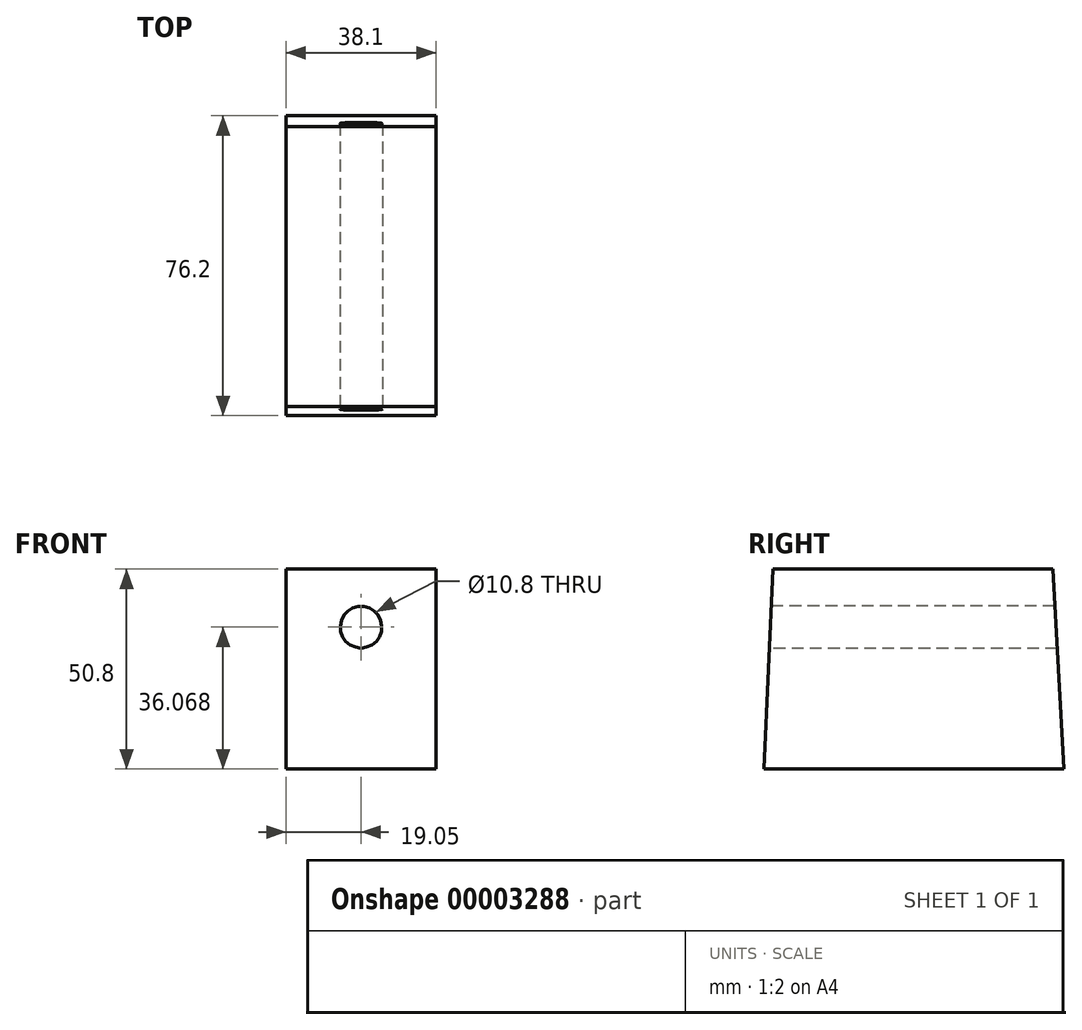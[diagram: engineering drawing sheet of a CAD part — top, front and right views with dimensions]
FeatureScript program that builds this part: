
annotation { "Feature Type Name" : "Feature", "Feature Type Description" : "" }
export const myFeature = defineFeature(function(context is Context, id is Id, definition is map)
    precondition{}
    {
        {
            var Q0;
            Q0=qCreatedBy(makeId("Top.planeOp"),FACE);
            var sketch = newSketch(context, id + "F0", { "sketchPlane" : qUnion([Q0])});
            skLineSegment(sketch, "E0", {"start": v(0, 0) * mm, "end": v(0, 76.2) * mm});
            skLineSegment(sketch, "E1", {"start": v(0, 76.2) * mm, "end": v(38.1, 76.2) * mm});
            skLineSegment(sketch, "E2", {"start": v(38.1, 76.2) * mm, "end": v(38.1, 0) * mm});
            skLineSegment(sketch, "E3", {"start": v(0, 0) * mm, "end": v(38.1, 0) * mm});
            skLineSegment(sketch, "E4", {"start": v(19.05, 0) * mm, "end": v(19.05, 76.2) * mm, "construction": true});
            skSolve(sketch);
        }
        {
            var Q0;
            Q0=makeQuery(id+"F0.imprint","IMPRINT",FACE,{"disambiguationData":[TD([[makeQuery(id+"F0.imprint","IMPRINT",EDGE,{"derivedFrom":sQuery(id+"F0.wireOp",EDGE,"E0")}),-1.0]])]});
            extrude(context, id + "F1", {"entities" : qUnion([Q0]), "depth" : 50.8 * mm});
        }
        {
            var Q0;
            Q0=makeQuery(id+"F1.opExtrude","SWEPT_FACE",FACE,{"disambiguationData":[OSD([sQuery(id+"F0.wireOp",EDGE,"E3")])]});
            var sketch = newSketch(context, id + "F2", { "sketchPlane" : qUnion([Q0])});
            skCircle(sketch, "E5", {"center": v(19.05, 36.07) * mm, "radius": 5.4 * mm});
            skCircle(sketch, "E6.0", {"center": v(19.05, 36.07) * mm, "radius": 11.75 * mm});
            skLineSegment(sketch, "E7", {"start": v(19.05, 50.8) * mm, "end": v(19.05, 0) * mm, "construction": true});
            skLineSegment(sketch, "E8", {"start": v(0, 22.73) * mm, "end": v(38.1, 22.73) * mm});
            skLineSegment(sketch, "E9", {"start": v(7.48, 38.11) * mm, "end": v(4.76, 22.73) * mm});
            skLineSegment(sketch, "E10", {"start": v(30.62, 38.11) * mm, "end": v(33.34, 22.73) * mm});
            skSolve(sketch);
        }
        {
            var Q0;
            Q0=makeQuery(id+"F2.imprint","IMPRINT",FACE,{"disambiguationData":[TD([[makeQuery(id+"F2.imprint","IMPRINT",EDGE,{"derivedFrom":sQuery(id+"F2.wireOp",EDGE,"E5")}),1.0]])]});
            var Q1;
            Q1=sQuery(id+"F2.wireOp",EDGE,"E5");
            extrude(context, id + "F3", {"entities" : qUnion([Q0]), "operationType" : NewBodyOperationType.REMOVE, "surfaceEntities" : qUnion([Q1]), "endBound" : BoundingType.THROUGH_ALL, "oppositeDirection" : true, "depth" : 25.4 * mm});
        }
        {
            var Q0;
            Q0=makeQuery(id+"F1.opExtrude","SWEPT_FACE",FACE,{"disambiguationData":[OSD([sQuery(id+"F0.wireOp",EDGE,"E1")])]});
            var sketch = newSketch(context, id + "F4", { "sketchPlane" : qUnion([Q0])});
            skSolve(sketch);
        }
        {
            var Q0;
            Q0=makeQuery(id+"F1.opExtrude","SWEPT_FACE",FACE,{"disambiguationData":[OSD([sQuery(id+"F0.wireOp",EDGE,"E2")])]});
            var sketch = newSketch(context, id + "F5", { "sketchPlane" : qUnion([Q0])});
            skLineSegment(sketch, "E11", {"start": v(73.4, 50.8) * mm, "end": v(76.2, 0) * mm});
            skLineSegment(sketch, "E12", {"start": v(2.3, 50.8) * mm, "end": v(0, 0) * mm});
            skSolve(sketch);
        }
        {
            var Q0;
            {var subQ2=sQuery(id+"F5.wireOp",EDGE,"E12");Q0=makeQuery(id+"F5.imprint","IMPRINT",FACE,{"disambiguationData":[TD([[makeQuery(id+"F5.imprint","IMPRINT",EDGE,{"derivedFrom":subQ2}),-1.0]])]});}
            var Q1;
            {var subQ2=sQuery(id+"F5.wireOp",EDGE,"E11");Q1=makeQuery(id+"F5.imprint","IMPRINT",FACE,{"disambiguationData":[TD([[makeQuery(id+"F5.imprint","IMPRINT",EDGE,{"derivedFrom":subQ2}),1.0]])]});}
            extrude(context, id + "F6", {"entities" : qUnion([Q0, Q1]), "operationType" : NewBodyOperationType.REMOVE, "oppositeDirection" : true, "depth" : 50.8 * mm});
        }
    });
